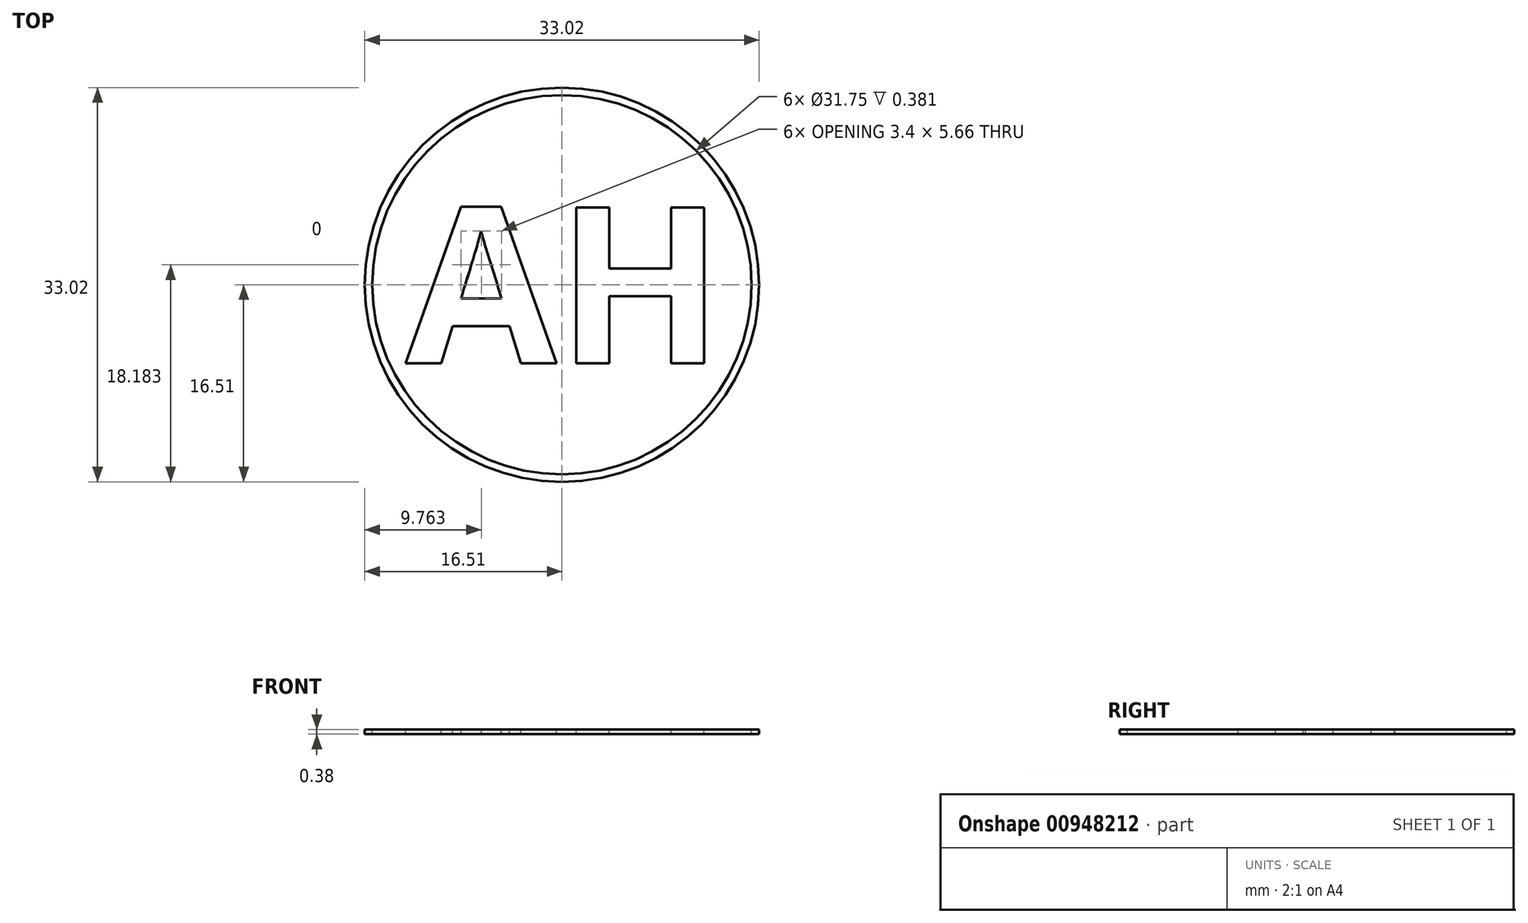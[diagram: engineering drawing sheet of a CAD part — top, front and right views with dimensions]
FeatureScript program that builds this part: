
annotation { "Feature Type Name" : "Feature", "Feature Type Description" : "" }
export const myFeature = defineFeature(function(context is Context, id is Id, definition is map)
    precondition{}
    {
        {
            var Q0;
            Q0=qCreatedBy(makeId("Top.planeOp"),FACE);
            cPlane(context, id + "F0", {"entities" : qUnion([Q0]), "cplaneType" : CPlaneType.OFFSET, "offset" : 3.3 * mm, "width" : 152.4 * mm, "height" : 152.4 * mm});
        }
        {
            var Q0;
            Q0=qCreatedBy(id+"F0.planeOp",FACE);
            var sketch = newSketch(context, id + "F1", { "sketchPlane" : qUnion([Q0])});
            skText(sketch, "E0", { "text": "AH", "fontName": "OpenSans-Bold.ttf"});
            const initialGuessF1  = {"E0": [-0.01308, -0.00659, 1, 0, 0.01318]};
            skSetInitialGuess(sketch, initialGuessF1);
            skSolve(sketch);
        }
        {
            var Q0;
            Q0=qCreatedBy(id+"F0.planeOp",FACE);
            var sketch = newSketch(context, id + "F2", { "sketchPlane" : qUnion([Q0])});
            skCircle(sketch, "E1", {"center": v(0, 0) * mm, "radius": 15.88 * mm});
            skCircle(sketch, "E2", {"center": v(0, 0) * mm, "radius": 16.51 * mm});
            skSolve(sketch);
        }
        {
            var Q0;
            Q0 = qSketchRegion(id + "F1", true);
            var Q1;
            Q1 = qSketchRegion(id + "F2", true);
            extrude(context, id + "F3", {"entities" : qUnion([Q0, Q1]), "oppositeDirection" : true, "depth" : 0.38 * mm, "offsetDistance" : 25.4 * mm});
        }
    });
